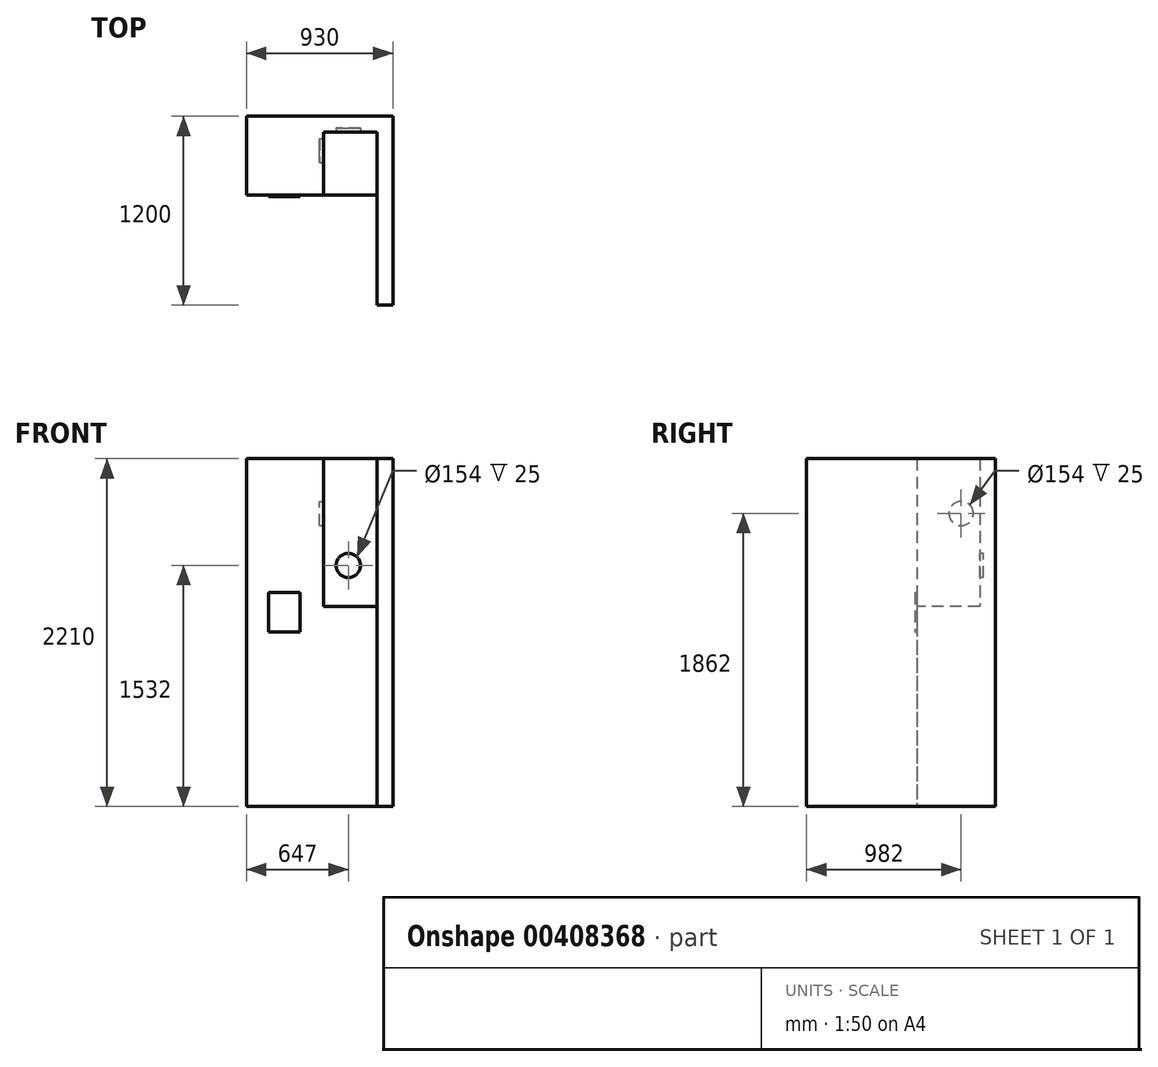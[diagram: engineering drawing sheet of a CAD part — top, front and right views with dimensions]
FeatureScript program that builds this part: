
annotation { "Feature Type Name" : "Feature", "Feature Type Description" : "" }
export const myFeature = defineFeature(function(context is Context, id is Id, definition is map)
    precondition{}
    {
        {
            var Q0;
            Q0=qCreatedBy(makeId("Top.planeOp"),FACE);
            var sketch = newSketch(context, id + "F0", { "sketchPlane" : qUnion([Q0])});
            skLineSegment(sketch, "E0.bottom", {"start": v(0, 0) * mm, "end": v(-830, 0) * mm});
            skLineSegment(sketch, "E0.left", {"start": v(0, 0) * mm, "end": v(0, -700) * mm});
            skLineSegment(sketch, "E1.bottom", {"start": v(100, 500) * mm, "end": v(-830, 500) * mm});
            skLineSegment(sketch, "E1.top", {"start": v(100, -700) * mm, "end": v(0, -700) * mm});
            skLineSegment(sketch, "E1.left", {"start": v(100, 500) * mm, "end": v(100, -700) * mm});
            skLineSegment(sketch, "E1.right", {"start": v(-830, 500) * mm, "end": v(-830, 0) * mm});
            skSolve(sketch);
        }
        {
            var Q0;
            Q0 = qSketchRegion(id + "F0", true);
            extrude(context, id + "F1", {"entities" : qUnion([Q0]), "depth" : (1270 + 940) * mm});
        }
        {
            var Q0;
            Q0=makeQuery(id+"F1.opExtrude","SWEPT_FACE",FACE,{"disambiguationData":[OSD([sQuery(id+"F0.wireOp",EDGE,"E0.bottom")])]});
            var sketch = newSketch(context, id + "F2", { "sketchPlane" : qUnion([Q0])});
            skLineSegment(sketch, "E2.bottom", {"start": v(0, 2210) * mm, "end": v(-340, 2210) * mm});
            skLineSegment(sketch, "E2.top", {"start": v(0, 1270) * mm, "end": v(-340, 1270) * mm});
            skLineSegment(sketch, "E2.left", {"start": v(0, 2210) * mm, "end": v(0, 1270) * mm});
            skLineSegment(sketch, "E2.right", {"start": v(-340, 2210) * mm, "end": v(-340, 1270) * mm});
            skSolve(sketch);
        }
        {
            var Q0;
            Q0=makeQuery(id+"F2.imprint","IMPRINT",FACE,{"disambiguationData":[TD([[makeQuery(id+"F2.imprint","IMPRINT",EDGE,{"derivedFrom":sQuery(id+"F2.wireOp",EDGE,"E2.bottom")}),1.0]])]});
            extrude(context, id + "F3", {"entities" : qUnion([Q0]), "operationType" : NewBodyOperationType.REMOVE, "oppositeDirection" : true, "depth" : 400 * mm});
        }
        {
            var Q0;
            Q0=makeQuery(id+"F3.boolean.opBoolean","COPY",FACE,{"derivedFrom":makeQuery(id+"F3.opExtrude","CAP_FACE",FACE,{"disambiguationData":[OSD([sQuery(id+"F2.wireOp",EDGE,"E2.bottom"),sQuery(id+"F2.wireOp",EDGE,"E2.top"),sQuery(id+"F2.wireOp",EDGE,"E2.left"),sQuery(id+"F2.wireOp",EDGE,"E2.right")])],"isStart":false})});
            var sketch = newSketch(context, id + "F4", { "sketchPlane" : qUnion([Q0])});
            skCircle(sketch, "E3", {"center": v(-183, 1532) * mm, "radius": 77 * mm});
            skSolve(sketch);
        }
        {
            var Q0;
            Q0=makeQuery(id+"F4.imprint","IMPRINT",FACE,{"disambiguationData":[TD([[makeQuery(id+"F4.imprint","IMPRINT",EDGE,{"derivedFrom":sQuery(id+"F4.wireOp",EDGE,"E3")}),1.0]])]});
            extrude(context, id + "F5", {"entities" : qUnion([Q0]), "operationType" : NewBodyOperationType.REMOVE, "oppositeDirection" : true, "depth" : 25 * mm});
        }
        {
            var Q0;
            Q0=makeQuery(id+"F3.boolean.opBoolean","COPY",FACE,{"derivedFrom":makeQuery(id+"F3.opExtrude","SWEPT_FACE",FACE,{"disambiguationData":[OSD([sQuery(id+"F2.wireOp",EDGE,"E2.right")])]})});
            var sketch = newSketch(context, id + "F6", { "sketchPlane" : qUnion([Q0])});
            skCircle(sketch, "E4", {"center": v(282, 1862) * mm, "radius": 77 * mm});
            skSolve(sketch);
        }
        {
            var Q0;
            Q0 = qSketchRegion(id + "F6", true);
            extrude(context, id + "F7", {"entities" : qUnion([Q0]), "operationType" : NewBodyOperationType.REMOVE, "oppositeDirection" : true, "depth" : 25 * mm});
        }
        {
            var Q0;
            {var subQ4=sQuery(id+"F2.wireOp",EDGE,"E2.top");Q0=makeQuery(id+"F2.imprint","IMPRINT",FACE,{"disambiguationData":[TD([[makeQuery(id+"F2.imprint","IMPRINT",EDGE,{"derivedFrom":subQ4}),1.0]])]});}
            var sketch = newSketch(context, id + "F8", { "sketchPlane" : qUnion([Q0])});
            skLineSegment(sketch, "E5.bottom", {"start": v(-690, 1360) * mm, "end": v(-490, 1360) * mm});
            skLineSegment(sketch, "E5.top", {"start": v(-690, 1110) * mm, "end": v(-490, 1110) * mm});
            skLineSegment(sketch, "E5.left", {"start": v(-690, 1360) * mm, "end": v(-690, 1110) * mm});
            skLineSegment(sketch, "E5.right", {"start": v(-490, 1360) * mm, "end": v(-490, 1110) * mm});
            skSolve(sketch);
        }
        {
            var Q0;
            Q0 = qSketchRegion(id + "F8", true);
            extrude(context, id + "F9", {"entities" : qUnion([Q0]), "operationType" : NewBodyOperationType.ADD, "depth" : 10 * mm});
        }
    });
